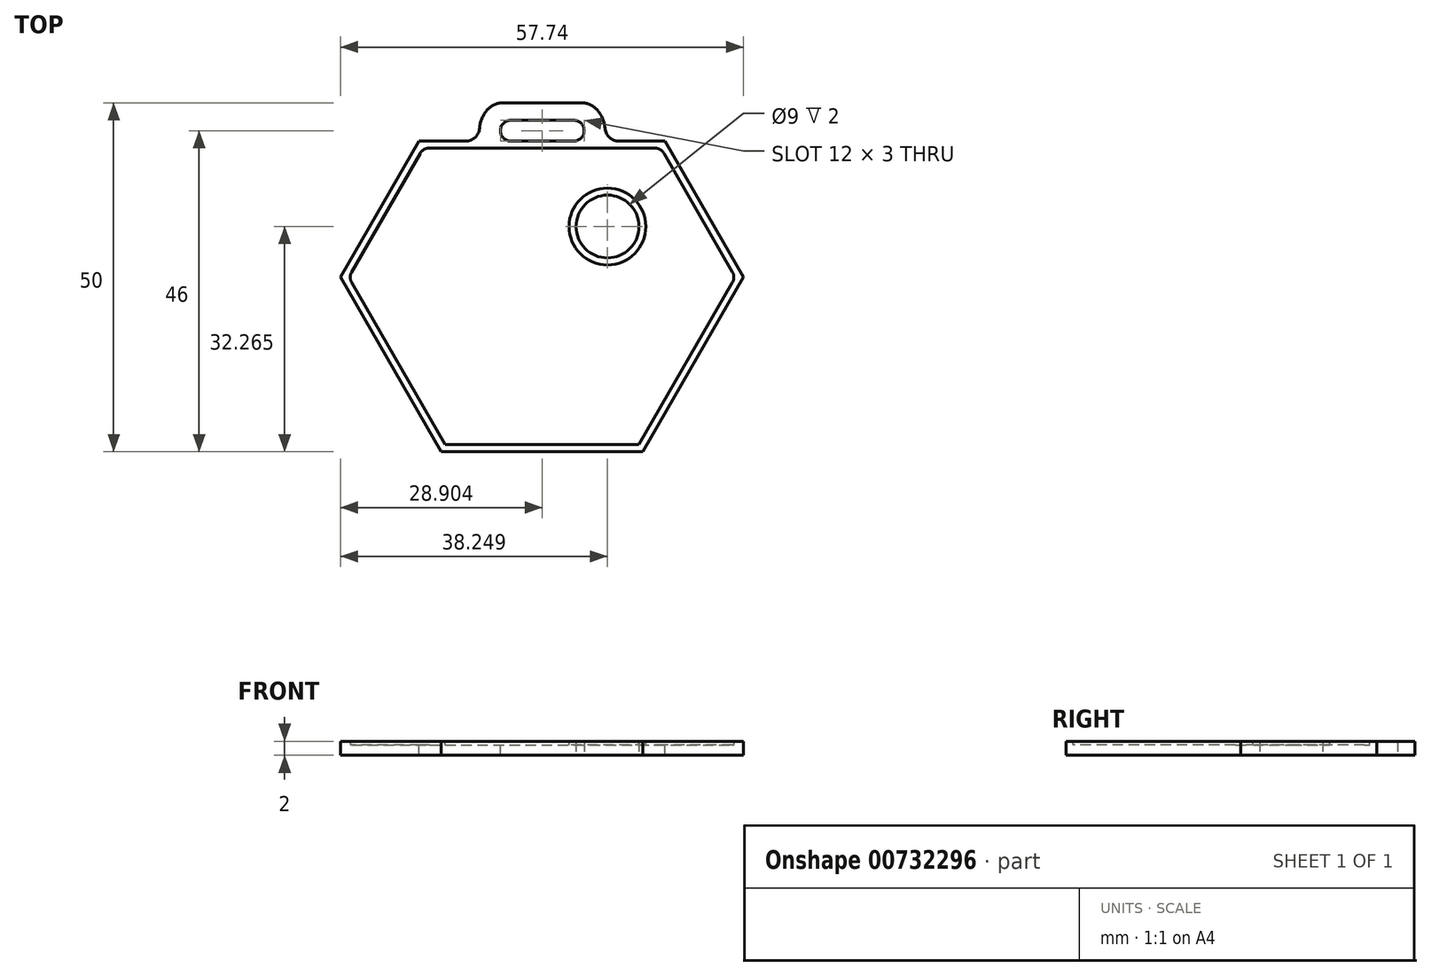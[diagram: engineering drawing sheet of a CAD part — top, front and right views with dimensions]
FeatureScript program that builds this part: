
annotation { "Feature Type Name" : "Feature", "Feature Type Description" : "" }
export const myFeature = defineFeature(function(context is Context, id is Id, definition is map)
    precondition{}
    {
        {
            var Q0;
            Q0=qCreatedBy(makeId("Top.planeOp"),FACE);
            var sketch = newSketch(context, id + "F0", { "sketchPlane" : qUnion([Q0])});
            skCircle(sketch, "E0.cCircle", {"center": v(0, 0) * mm, "radius": 25 * mm, "construction": true});
            skLineSegment(sketch, "E0.0", {"start": v(28.87, 0) * mm, "end": v(14.43, -25) * mm});
            skLineSegment(sketch, "E0.1", {"start": v(14.43, -25) * mm, "end": v(-14.43, -25) * mm});
            skLineSegment(sketch, "E0.2", {"start": v(-14.43, -25) * mm, "end": v(-28.87, 0) * mm});
            skLineSegment(sketch, "E0.3", {"start": v(-28.87, 0) * mm, "end": v(-14.43, 25) * mm});
            skLineSegment(sketch, "E0.4", {"start": v(-14.43, 25) * mm, "end": v(14.43, 25) * mm});
            skLineSegment(sketch, "E0.5", {"start": v(14.43, 25) * mm, "end": v(28.87, 0) * mm});
            skPoint(sketch, "E0.0.midPoint", {"position": v(21.65, -12.5) * mm});
            skCircle(sketch, "E1", {"center": v(9.38, 7.26) * mm, "radius": 4.5 * mm});
            skLineSegment(sketch, "E2.bottom", {"start": v(-5.97, 22.5) * mm, "end": v(6.03, 22.5) * mm});
            skLineSegment(sketch, "E2.top", {"start": v(-5.97, 19.5) * mm, "end": v(6.03, 19.5) * mm});
            skLineSegment(sketch, "E2.left", {"start": v(-5.97, 22.5) * mm, "end": v(-5.97, 19.5) * mm});
            skLineSegment(sketch, "E2.right", {"start": v(6.03, 22.5) * mm, "end": v(6.03, 19.5) * mm});
            skSolve(sketch);
        }
        {
            var Q0;
            Q0 = qSketchRegion(id + "F0", true);
            extrude(context, id + "F1", {"entities" : qUnion([Q0]), "depth" : 2 * mm, "offsetDistance" : 25 * mm});
        }
        {
            var Q0;
            Q0=makeQuery(id+"F1.opExtrude","CAP_FACE",FACE,{"disambiguationData":[OSD([sQuery(id+"F0.wireOp",EDGE,"E0.0"),sQuery(id+"F0.wireOp",EDGE,"E0.1"),sQuery(id+"F0.wireOp",EDGE,"E0.2"),sQuery(id+"F0.wireOp",EDGE,"E0.3"),sQuery(id+"F0.wireOp",EDGE,"E0.4"),sQuery(id+"F0.wireOp",EDGE,"E0.5"),sQuery(id+"F0.wireOp",EDGE,"E1"),sQuery(id+"F0.wireOp",EDGE,"E2.bottom"),sQuery(id+"F0.wireOp",EDGE,"E2.top"),sQuery(id+"F0.wireOp",EDGE,"E2.left"),sQuery(id+"F0.wireOp",EDGE,"E2.right")])],"isStart":false});
            var sketch = newSketch(context, id + "F2", { "sketchPlane" : qUnion([Q0])});
            skCircle(sketch, "E3.0", {"center": v(9.38, 7.26) * mm, "radius": 5.5 * mm});
            skLineSegment(sketch, "E4.0", {"start": v(13.86, -24) * mm, "end": v(27.71, 0) * mm});
            skLineSegment(sketch, "E4.1", {"start": v(13.86, 24) * mm, "end": v(-13.86, 24) * mm});
            skLineSegment(sketch, "E4.2", {"start": v(-17.03, 18.5) * mm, "end": v(-27.71, 0) * mm});
            skLineSegment(sketch, "E4.3", {"start": v(27.71, 0) * mm, "end": v(17.03, 18.5) * mm});
            skLineSegment(sketch, "E4.4", {"start": v(-27.71, 0) * mm, "end": v(-13.86, -24) * mm});
            skLineSegment(sketch, "E4.5", {"start": v(-13.86, -24) * mm, "end": v(13.86, -24) * mm});
            skLineSegment(sketch, "E5", {"start": v(-17.03, 18.5) * mm, "end": v(17.03, 18.5) * mm});
            skSolve(sketch);
        }
        {
            var Q0;
            Q0 = qSketchRegion(id + "F2", true);
            extrude(context, id + "F3", {"entities" : qUnion([Q0]), "operationType" : NewBodyOperationType.REMOVE, "oppositeDirection" : true, "depth" : 0.5 * mm, "offsetDistance" : 25 * mm});
        }
        {
            var Q0;
            Q0=makeQuery(id+"F3.boolean.opBoolean","COPY",FACE,{"derivedFrom":makeQuery(id+"F3.opExtrude","CAP_FACE",FACE,{"disambiguationData":[OSD([sQuery(id+"F2.wireOp",EDGE,"E3.0"),sQuery(id+"F2.wireOp",EDGE,"E4.0"),sQuery(id+"F2.wireOp",EDGE,"E4.2"),sQuery(id+"F2.wireOp",EDGE,"E4.3"),sQuery(id+"F2.wireOp",EDGE,"E4.4"),sQuery(id+"F2.wireOp",EDGE,"E4.5"),sQuery(id+"F2.wireOp",EDGE,"E5")])],"isStart":false})});
            var sketch = newSketch(context, id + "F4", { "sketchPlane" : qUnion([Q0])});
            skSolve(sketch);
        }
        {
            var Q0;
            Q0=makeQuery(id+"F1.opExtrude","SWEPT_EDGE",EDGE,{"disambiguationData":[OSD([sQuery(id+"F0.wireOp",EDGE,"E2.top"),sQuery(id+"F0.wireOp",EDGE,"E2.left")])]});
            var Q1;
            Q1=makeQuery(id+"F1.opExtrude","SWEPT_EDGE",EDGE,{"disambiguationData":[OSD([sQuery(id+"F0.wireOp",EDGE,"E2.top"),sQuery(id+"F0.wireOp",EDGE,"E2.right")])]});
            var Q2;
            Q2=makeQuery(id+"F1.opExtrude","SWEPT_EDGE",EDGE,{"disambiguationData":[OSD([sQuery(id+"F0.wireOp",EDGE,"E2.bottom"),sQuery(id+"F0.wireOp",EDGE,"E2.right")])]});
            var Q3;
            Q3=makeQuery(id+"F1.opExtrude","SWEPT_EDGE",EDGE,{"disambiguationData":[OSD([sQuery(id+"F0.wireOp",EDGE,"E2.bottom"),sQuery(id+"F0.wireOp",EDGE,"E2.left")])]});
            var Q4;
            Q4=makeQuery(id+"F3.boolean.opBoolean","COPY",EDGE,{"derivedFrom":makeQuery(id+"F3.opExtrude","SWEPT_EDGE",EDGE,{"disambiguationData":[OSD([sQuery(id+"F2.wireOp",EDGE,"E4.2"),sQuery(id+"F2.wireOp",EDGE,"E5")])]})});
            var Q5;
            Q5=makeQuery(id+"F3.boolean.opBoolean","COPY",EDGE,{"derivedFrom":makeQuery(id+"F3.opExtrude","SWEPT_EDGE",EDGE,{"disambiguationData":[OSD([sQuery(id+"F2.wireOp",EDGE,"E4.2"),sQuery(id+"F2.wireOp",EDGE,"E4.4")])]})});
            var Q6;
            Q6=makeQuery(id+"F3.boolean.opBoolean","COPY",EDGE,{"derivedFrom":makeQuery(id+"F3.opExtrude","SWEPT_EDGE",EDGE,{"disambiguationData":[OSD([sQuery(id+"F2.wireOp",EDGE,"E4.3"),sQuery(id+"F2.wireOp",EDGE,"E5")])]})});
            var Q7;
            Q7=makeQuery(id+"F3.boolean.opBoolean","COPY",EDGE,{"derivedFrom":makeQuery(id+"F3.opExtrude","SWEPT_EDGE",EDGE,{"disambiguationData":[OSD([sQuery(id+"F2.wireOp",EDGE,"E4.0"),sQuery(id+"F2.wireOp",EDGE,"E4.3")])]})});
            fillet(context, id + "F5", {"entities" : qUnion([Q0, Q1, Q2, Q3, Q4, Q5, Q6, Q7]), "radius" : 1.5 * mm, "tangentPropagation" : true, "allowEdgeOverflow" : false});
        }
        {
            var Q0;
            {var subQ0=sQuery(id+"F0.wireOp",EDGE,"E2.right");var subQ1=sQuery(id+"F0.wireOp",EDGE,"E2.top");var subQ2=sQuery(id+"F0.wireOp",EDGE,"E2.bottom");var subQ3=sQuery(id+"F0.wireOp",EDGE,"E0.5");var subQ4=sQuery(id+"F0.wireOp",EDGE,"E0.4");var subQ5=sQuery(id+"F0.wireOp",EDGE,"E2.left");var subQ6=sQuery(id+"F0.wireOp",EDGE,"E0.0");var subQ7=sQuery(id+"F0.wireOp",EDGE,"E0.3");var subQ8=sQuery(id+"F0.wireOp",EDGE,"E0.1");var subQ9=sQuery(id+"F0.wireOp",EDGE,"E0.2");Q0=makeQuery(id+"F3.boolean.opBoolean","SPLIT",FACE,{"disambiguationData":[TD([makeQuery(id+"F1.opExtrude","SWEPT_FACE",FACE,{"disambiguationData":[OSD([subQ6])]})])],"derivedFrom":makeQuery(id+"F1.opExtrude","CAP_FACE",FACE,{"disambiguationData":[OSD([subQ6,subQ8,subQ9,subQ7,subQ4,subQ3,sQuery(id+"F0.wireOp",EDGE,"E1"),subQ2,subQ1,subQ5,subQ0])],"isStart":false})});}
            var sketch = newSketch(context, id + "F6", { "sketchPlane" : qUnion([Q0])});
            skArc(sketch, "E6.0", {"start": v(4.53, 25.5) * mm, "mid": v(7.6, 24.3) * mm, "end": v(9.02, 21.35) * mm});
            skLineSegment(sketch, "E6.1", {"start": v(-4.47, 25.5) * mm, "end": v(4.53, 25.5) * mm});
            skArc(sketch, "E6.2", {"start": v(-8.95, 21.35) * mm, "mid": v(-7.52, 24.3) * mm, "end": v(-4.47, 25.5) * mm});
            skLineSegment(sketch, "E7.1", {"start": v(-17.6, 19.5) * mm, "end": v(-28.87, 0) * mm});
            skLineSegment(sketch, "E7.2", {"start": v(-28.87, 0) * mm, "end": v(-14.43, -25) * mm});
            skLineSegment(sketch, "E7.3", {"start": v(21.36, 19.5) * mm, "end": v(11.01, 19.5) * mm});
            skLineSegment(sketch, "E7.4", {"start": v(-14.43, -25) * mm, "end": v(14.43, -25) * mm});
            skLineSegment(sketch, "E7.5", {"start": v(14.43, -25) * mm, "end": v(30.31, 2.5) * mm});
            skLineSegment(sketch, "E8", {"start": v(-17.6, 19.5) * mm, "end": v(-20.35, 30.28) * mm});
            skLineSegment(sketch, "E9", {"start": v(-20.35, 30.28) * mm, "end": v(25.7, 29.27) * mm});
            skLineSegment(sketch, "E10", {"start": v(25.7, 29.27) * mm, "end": v(21.36, 19.5) * mm});
            skLineSegment(sketch, "E11.trimOffspring", {"start": v(-10.95, 19.5) * mm, "end": v(-17.6, 19.5) * mm});
            skPoint(sketch, "E12.visualSharp", {"position": v(-8.7, 19.5) * mm});
            skArc(sketch, "E12.filletArc", {"start": v(-10.95, 19.5) * mm, "mid": v(-9.59, 20.03) * mm, "end": v(-8.95, 21.35) * mm});
            skPoint(sketch, "E13.visualSharp", {"position": v(8.78, 19.5) * mm});
            skArc(sketch, "E13.filletArc", {"start": v(9.02, 21.35) * mm, "mid": v(9.66, 20.03) * mm, "end": v(11.01, 19.5) * mm});
            skSolve(sketch);
        }
        {
            var Q0;
            Q0 = qSketchRegion(id + "F6", true);
            extrude(context, id + "F7", {"entities" : qUnion([Q0]), "operationType" : NewBodyOperationType.REMOVE, "oppositeDirection" : true, "depth" : 25 * mm, "offsetDistance" : 25 * mm});
        }
        {
            var Q0;
            Q0=makeQuery(id+"F7.boolean.opBoolean","INTERSECT",EDGE,{"derivedFrom":[makeQuery(id+"F1.opExtrude","SWEPT_FACE",FACE,{"disambiguationData":[OSD([sQuery(id+"F0.wireOp",EDGE,"E0.4")])]}),makeQuery(id+"F7.opExtrude","SWEPT_FACE",FACE,{"disambiguationData":[OSD([sQuery(id+"F6.wireOp",EDGE,"E6.2")])]})]});
            var Q1;
            Q1=makeQuery(id+"F7.boolean.opBoolean","INTERSECT",EDGE,{"derivedFrom":[makeQuery(id+"F1.opExtrude","SWEPT_FACE",FACE,{"disambiguationData":[OSD([sQuery(id+"F0.wireOp",EDGE,"E0.4")])]}),makeQuery(id+"F7.opExtrude","SWEPT_FACE",FACE,{"disambiguationData":[OSD([sQuery(id+"F6.wireOp",EDGE,"E6.0")])]})]});
            fillet(context, id + "F8", {"entities" : qUnion([Q0, Q1]), "radius" : 3 * mm, "tangentPropagation" : true, "allowEdgeOverflow" : false});
        }
    });
